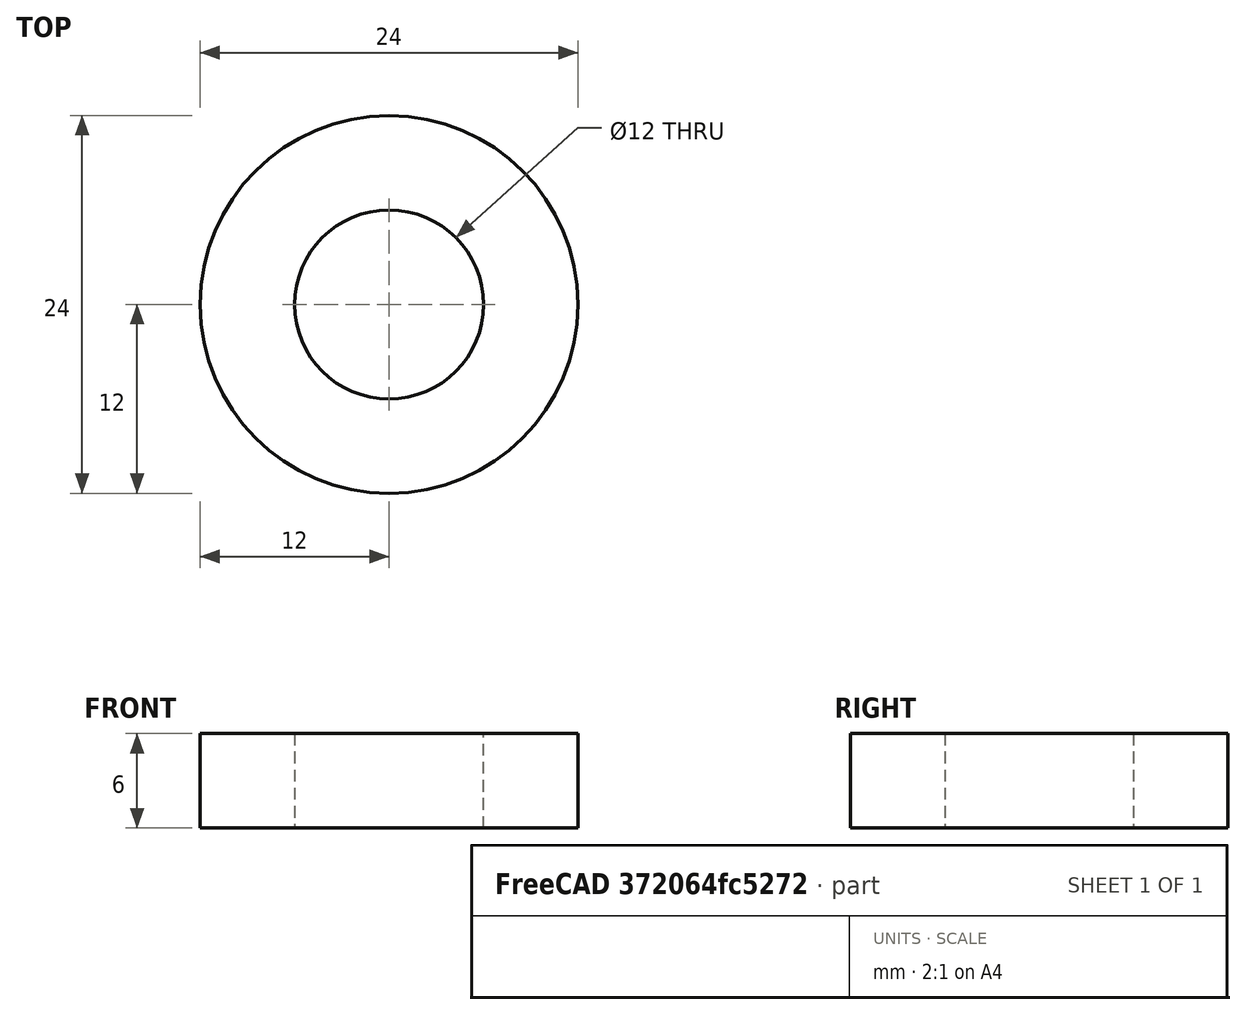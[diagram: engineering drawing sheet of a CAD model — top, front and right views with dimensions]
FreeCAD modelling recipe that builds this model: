
FCSTD DOCUMENT  (FreeCAD 0.17R13522 (Git))
Label: Bearing
License: All rights reserved
LicenseURL: http://en.wikipedia.org/wiki/All_rights_reserved
objects: Sketcher::SketchObject×1, PartDesign::Pad×1, PartDesign::Body×1, App::Part×1
note: 4 computed .brp shape members not serialized (recipe doc carries the construction recipe); baked Part::Feature solids carry a one-line shape summary decoded from their .brp

FEATURE [Sketcher::SketchObject] Sketch
  MapMode = 5
  Support = -> [XY_Plane001]
  sketch-geometry (2):
    g0: Circle CenterX=0 CenterY=0 CenterZ=0 NormalX=0 NormalY=0 NormalZ=1 AngleXU=0 Radius=6
    g1: Circle CenterX=0 CenterY=0 CenterZ=0 NormalX=0 NormalY=0 NormalZ=1 AngleXU=0 Radius=12
  constraints (4):
    c: Coincident(g0,g-1)
    c: Coincident(g1,g-1)
    c: Radius(g1) = 12
    c: Radius(g0) = 6
FEATURE [PartDesign::Pad] Pad
  Length = 6
  Length2 = 100
  Profile = -> Sketch
  Type = 0
FEATURE [PartDesign::Body] Body
  Group = -> [Sketch,Pad]
  Origin = -> Origin001
  Tip = -> Pad
FEATURE [App::Part] Part
  Group = -> [Body]
  License = CC BY 3.0
  LicenseURL = http://creativecommons.org/licenses/by/3.0/
  Origin = -> Origin
